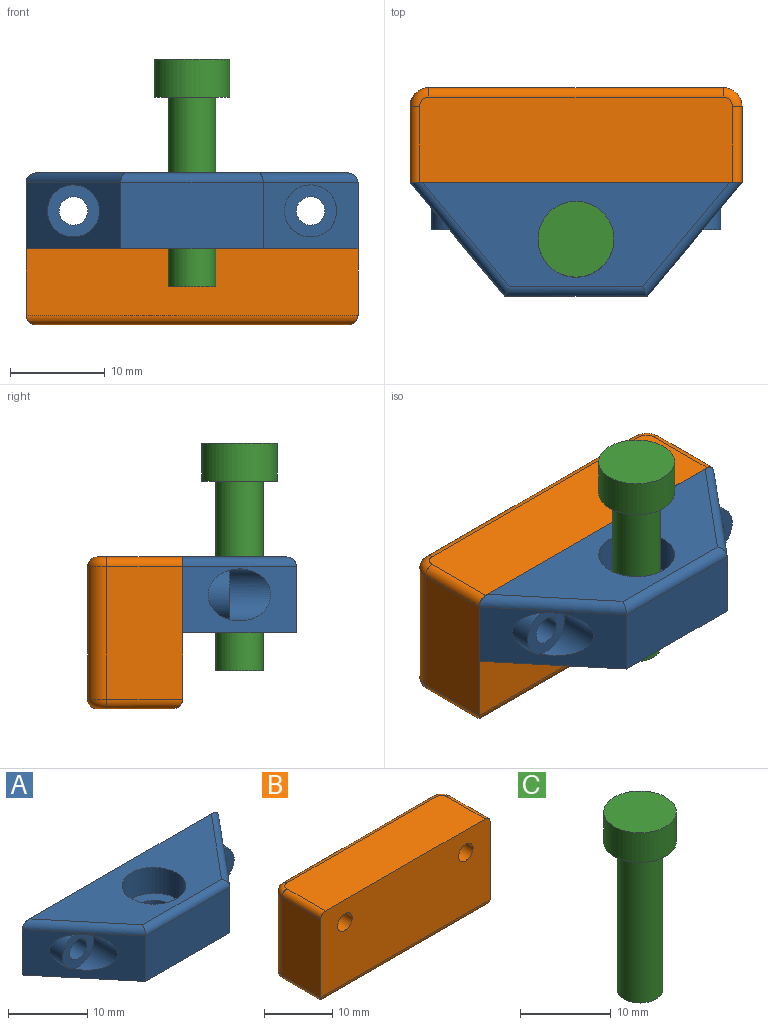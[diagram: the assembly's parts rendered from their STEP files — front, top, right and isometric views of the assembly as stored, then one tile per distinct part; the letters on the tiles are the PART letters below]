
ASSEMBLY  parts=3 mates=2
PART A: 20 faces, bbox 35x12.6x8 mm
  f0: cylinder r=1.5mm len=5mm, axis (0,1,0), area 47.1mm2, adj f4,f12
  f1: cylinder r=1.5mm len=5mm, axis (0,1,0), area 47.1mm2, adj f4,f14
  f2: plane 12x10mm, normal (-0.77,-0.64,0), area 72.2mm2, adj f4,f5,f8,f13,f15,f17
  f3: plane 12x10mm, normal (0.77,-0.64,0), area 72.2mm2, adj f4,f5,f8,f11,f16,f18
  f4: plane 35x8mm, normal (0,1,0), area 265.3mm2, adj f0,f1,f2,f3,f7,f8,f17,f18
  f5: plane 15x7mm, normal (0,-1,0), area 105mm2, adj f2,f3,f8,f19
  f6: cylinder r=4mm len=8mm, axis (0,0,-1), area 100.5mm2, adj f7,f10
  f7: plane 32.4x11mm, normal (0,0,1), area 205.3mm2, adj f4,f6,f17,f18,f19
  f8: plane 35x12mm, normal (0,0,-1), area 280.4mm2, adj f2,f3,f4,f5,f9
  f9: cylinder r=2.5mm len=5mm, axis (0,0,-1), area 62.8mm2, adj f8,f10
  f10: plane 8x8mm, normal (0,0,1), area 30.6mm2, adj f6,f9
  f11: cylinder r=2.75mm len=5.24mm, axis (0,1,0), area 10.4mm2, adj f3,f12
  f12: plane 5.5x5.5mm, normal (0,-1,0), area 16.7mm2, adj f0,f11,f16
  f13: cylinder r=2.75mm len=5.24mm, axis (0,1,0), area 10.4mm2, adj f2,f14
  f14: plane 5.5x5.5mm, normal (0,-1,0), area 16.7mm2, adj f1,f13,f15
  f15: cylinder r=2.75mm len=5.5mm, axis (0,1,0), area 27.6mm2, adj f2,f14
  f16: cylinder r=2.75mm len=5.5mm, axis (0,1,0), area 27.6mm2, adj f3,f12
  f17: cylinder r=1mm len=12.64mm, axis (-0.64,0.77,0), area 23.8mm2, adj f2,f4,f7,f19
  f18: cylinder r=1mm len=12.64mm, axis (-0.64,-0.77,0), area 23.8mm2, adj f3,f4,f7,f19
  f19: cylinder r=1mm len=15mm, axis (-1,0,0), area 23mm2, adj f5,f7,f17,f18
PART B: 33 faces, bbox 35.3x10.2x16 mm
  f0: cylinder r=2mm len=14mm, axis (0,0,-1), area 44mm2, adj f1,f5,f25,f31
  f1: plane 14x8mm, normal (-1,0,0), area 112mm2, adj f0,f2,f27,f32
  f2: plane 35x15mm, normal (0,-1,0), area 510.4mm2, adj f1,f3,f6,f8,f9,f26,f28,f32
  f3: plane 14x8mm, normal (1,0,0), area 112mm2, adj f2,f4,f24,f28
  f4: cylinder r=2mm len=14mm, axis (0,0,-1), area 44mm2, adj f3,f5,f22,f29
  f5: plane 31x14mm, normal (0,1,0), area 377.5mm2, adj f0,f4,f8,f9,f10,f12,f14,f16
  f6: plane 33x9mm, normal (0,0,1), area 296.6mm2, adj f2,f28,f29,f30,f31,f32
  f7: plane 33x8mm, normal (0,0,-1), area 263.6mm2, adj f22,f23,f24,f25,f26,f27
  f8: cylinder r=1.5mm len=10mm, axis (0,1,0), area 94.2mm2, adj f2,f5
  f9: cylinder r=1.5mm len=10mm, axis (0,1,0), area 94.2mm2, adj f2,f5
  f10: cylinder r=1.5mm len=5mm, axis (0,1,0), area 47.1mm2, adj f5,f11
  f11: plane 3x3mm, normal (0,1,0), area 7.1mm2, adj f10
  f12: cylinder r=1.5mm len=5mm, axis (0,1,0), area 47.1mm2, adj f5,f13
  f13: plane 3x3mm, normal (0,1,0), area 7.1mm2, adj f12
  f14: cylinder r=1.5mm len=5mm, axis (0,1,0), area 47.1mm2, adj f5,f15
  f15: plane 3x3mm, normal (0,1,0), area 7.1mm2, adj f14
  f16: cylinder r=1.5mm len=5mm, axis (0,1,0), area 47.1mm2, adj f5,f17
  f17: plane 3x3mm, normal (0,1,0), area 7.1mm2, adj f16
  f18: cylinder r=1.5mm len=5mm, axis (0,1,0), area 47.1mm2, adj f5,f19
  f19: plane 3x3mm, normal (0,1,0), area 7.1mm2, adj f18
  f20: cylinder r=1.5mm len=5mm, axis (0,1,0), area 47.1mm2, adj f5,f21
  f21: plane 3x3mm, normal (0,1,0), area 7.1mm2, adj f20
  f22: torus R=1mm, axis (0,0,1), area 4mm2, adj f4,f7,f23,f24
  f23: cylinder r=1mm len=31mm, axis (-1,0,0), area 48.7mm2, adj f5,f7,f22,f25
  f24: cylinder r=1mm len=8mm, axis (0,1,0), area 12mm2, adj f3,f7,f22,f26
  f25: torus R=1mm, axis (0,0,1), area 4mm2, adj f0,f7,f23,f27
  f26: cylinder r=1mm len=35mm, axis (1,0,0), area 53.8mm2, adj f2,f7,f24,f27
  f27: cylinder r=1mm len=8mm, axis (0,-1,0), area 12mm2, adj f1,f7,f25,f26
  f28: cylinder r=1mm len=8mm, axis (0,-1,0), area 12.6mm2, adj f2,f3,f6,f29
  f29: torus R=1mm, axis (0,0,1), area 4mm2, adj f4,f6,f28,f30
  f30: cylinder r=1mm len=31mm, axis (1,0,0), area 48.7mm2, adj f5,f6,f29,f31
  f31: torus R=1mm, axis (0,0,1), area 4mm2, adj f0,f6,f30,f32
  f32: cylinder r=1mm len=8mm, axis (0,1,0), area 12.6mm2, adj f1,f2,f6,f31
PART C: 5 faces, bbox 8x8x24 mm
  f0: cylinder r=2.5mm len=20mm, axis (0,0,-1), area 314.2mm2, adj f1,f4
  f1: plane 5x5mm, normal (0,0,-1), area 19.6mm2, adj f0
  f2: cylinder r=4mm len=8mm, axis (0,0,-1), area 100.5mm2, adj f3,f4
  f3: plane 8x8mm, normal (0,0,1), area 50.3mm2, adj f2
  f4: plane 8x8mm, normal (0,0,-1), area 30.6mm2, adj f0,f2
PLACE A t=(5.59,0.35,0.67)mm fixed
PLACE B t=(5.59,0.35,0.67)mm
PLACE C t=(5.59,0.35,-3.34)mm
MATE slider A.f6 <-> C.f0  axis (0,0,1) through (13.09,6.35,4.67)mm
MATE fastened A.f4 <-> B.f2  axis (0,1,0) through (13.09,12.35,8.67)mm
